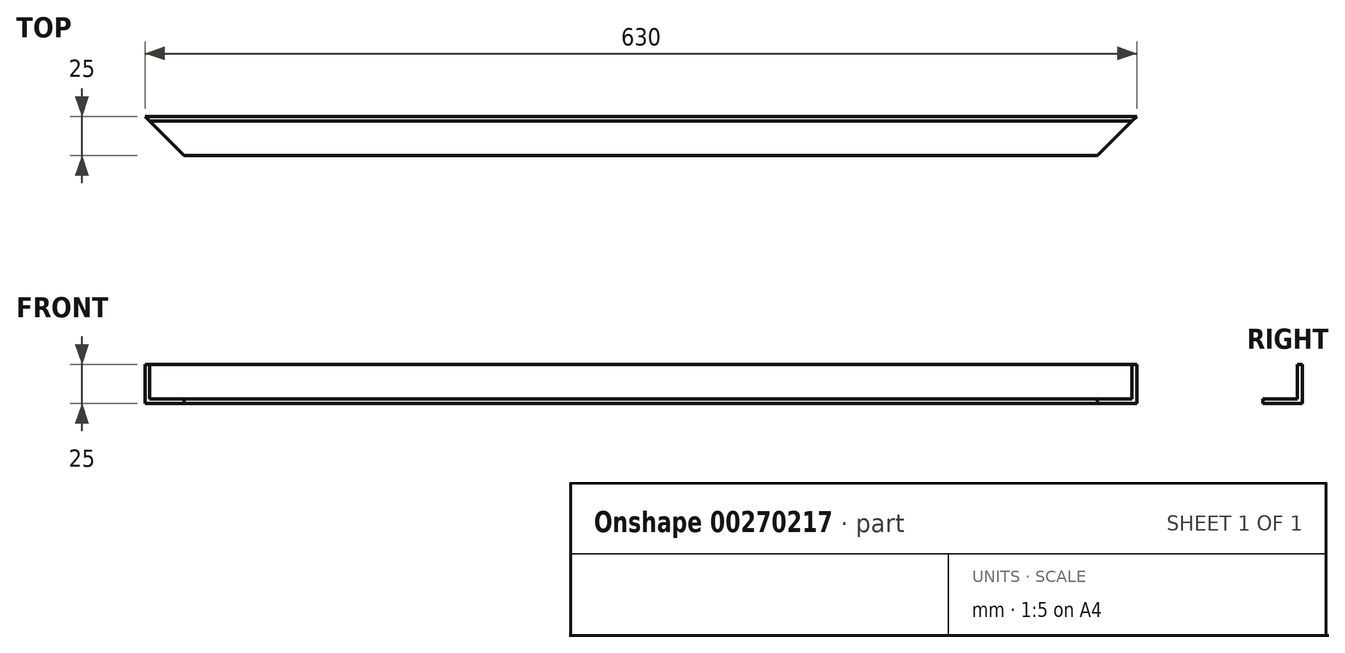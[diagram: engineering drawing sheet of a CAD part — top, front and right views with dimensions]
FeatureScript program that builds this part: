
annotation { "Feature Type Name" : "Feature", "Feature Type Description" : "" }
export const myFeature = defineFeature(function(context is Context, id is Id, definition is map)
    precondition{}
    {
        {
            var Q0;
            Q0=qCreatedBy(makeId("Right.planeOp"),FACE);
            var sketch = newSketch(context, id + "F0", { "sketchPlane" : qUnion([Q0])});
            skLineSegment(sketch, "E0", {"start": v(0, 0) * mm, "end": v(25, 0) * mm});
            skLineSegment(sketch, "E1", {"start": v(25, 0) * mm, "end": v(25, 25) * mm});
            skLineSegment(sketch, "E2", {"start": v(25, 25) * mm, "end": v(22, 25) * mm});
            skLineSegment(sketch, "E3", {"start": v(22, 25) * mm, "end": v(22, 3) * mm});
            skLineSegment(sketch, "E4", {"start": v(22, 3) * mm, "end": v(0, 3) * mm});
            skLineSegment(sketch, "E5", {"start": v(0, 3) * mm, "end": v(0, 0) * mm});
            skSolve(sketch);
        }
        {
            var Q0;
            Q0=makeQuery(id+"F0.imprint","IMPRINT",FACE,{"disambiguationData":[TD([[makeQuery(id+"F0.imprint","IMPRINT",EDGE,{"derivedFrom":sQuery(id+"F0.wireOp",EDGE,"E0")}),1.0]])]});
            extrude(context, id + "F1", {"entities" : qUnion([Q0]), "depth" : 634 * mm});
        }
        {
            var Q0;
            Q0=makeQuery(id+"F1.opExtrude","CAP_EDGE",EDGE,{"disambiguationData":[OSD([sQuery(id+"F0.wireOp",EDGE,"E3")])],"isStart":false});
            var Q1;
            Q1=makeQuery(id+"F1.opExtrude","CAP_EDGE",EDGE,{"disambiguationData":[OSD([sQuery(id+"F0.wireOp",EDGE,"E3")])],"isStart":true});
            chamfer(context, id + "F2", {"entities" : qUnion([Q0, Q1]), "width" : 5 * mm, "tangentPropagation" : true});
        }
        {
            var Q0;
            Q0=makeQuery(id+"F1.opExtrude","SWEPT_FACE",FACE,{"disambiguationData":[OSD([sQuery(id+"F0.wireOp",EDGE,"E4")])]});
            var sketch = newSketch(context, id + "F3", { "sketchPlane" : qUnion([Q0])});
            skLineSegment(sketch, "E6", {"start": v(2, 25) * mm, "end": v(27, 0) * mm});
            skLineSegment(sketch, "E7", {"start": v(632, 25) * mm, "end": v(607, 0) * mm});
            skSolve(sketch);
        }
        {
            var Q0;
            {var subQ0=sQuery(id+"F0.wireOp",EDGE,"E4");var subQ3=makeQuery(id+"F1.opExtrude","CAP_EDGE",EDGE,{"disambiguationData":[OSD([subQ0])],"isStart":false});Q0=makeQuery(id+"F3.imprint","IMPRINT",FACE,{"disambiguationData":[TD([[makeQuery(id+"F3.imprint","IMPRINT",EDGE,{"derivedFrom":subQ3}),-1.0]])]});}
            var Q1;
            {var subQ0=sQuery(id+"F0.wireOp",EDGE,"E4");var subQ1=makeQuery(id+"F1.opExtrude","CAP_EDGE",EDGE,{"disambiguationData":[OSD([subQ0])],"isStart":true});Q1=makeQuery(id+"F3.imprint","IMPRINT",FACE,{"disambiguationData":[TD([[makeQuery(id+"F3.imprint","IMPRINT",EDGE,{"derivedFrom":subQ1}),1.0]])]});}
            extrude(context, id + "F4", {"entities" : qUnion([Q0, Q1]), "operationType" : NewBodyOperationType.REMOVE, "oppositeDirection" : true, "depth" : 25 * mm});
        }
    });
